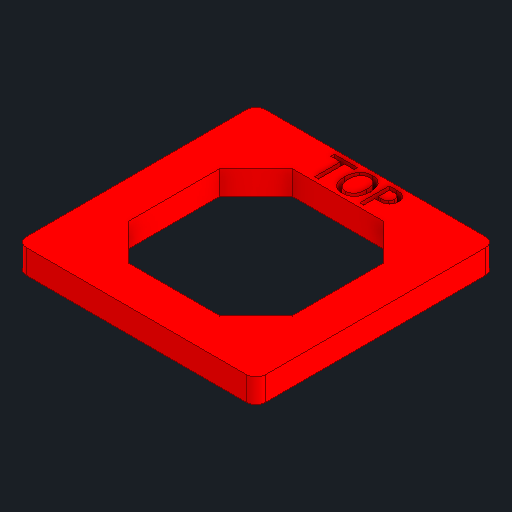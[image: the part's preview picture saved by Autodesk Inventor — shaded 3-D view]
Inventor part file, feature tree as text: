
AUTODESK INVENTOR PART (.ipt)
format: ipt  version: 2023.4 (Build 274418000, 418)  size: 544,256 bytes
history: native  units: mm
features: extrude x9, projected_geometry x9, chamfer x3, fillet x1, pattern_circular x1, sketch x1
ambient origin geometry x8: Origin, YZ Plane, XZ Plane, XY Plane, X Axis, Y Axis, Z Axis, Center Point
bodies: Solid1 (feature_tree)
feature tree (24):
  extrude  "Extrusion1"  Depth=49.8mm
  extrude  "Extrusion2"  Depth=7.85mm
  chamfer  "Chamfer1"  Distance=3.0mm
  fillet  "Fillet1"  Radius=3.0mm
  chamfer  "Chamfer2"  Distance=3.75mm
  extrude  "Extrusion3"  Depth=4.2125mm
  extrude  "Extrusion4"  Depth=0.675mm
  extrude  "Extrusion5"  Depth=10.5mm
  pattern_circular  "Circular Pattern1"  [2 undecoded]
  extrude  "Extrusion6"  Depth=4.1mm
  extrude  "Extrusion7"  Depth=4.145mm
  chamfer  "Chamfer3"  Distance=7.85mm
  extrude  "Extrusion8"  Depth=7.85mm
  extrude  "Extrusion9"  Depth=5.5mm
  sketch  "Sketch2"  dims[d0=49.8mm d1=49.8mm d2=7.85mm d3=3.0mm d4=3.0mm d5=3.75mm d6=4.2125mm d7=0.675mm d8=10.5mm d9=10.5mm d10=4.1mm d11=4.145mm d12=7.85mm d13=7.85mm d14=5.5mm d15=5.5mm d16=40.0mm d18=360.0deg d20=7.7mm d21=0.0mm d22=2.2mm d23=0.0mm d24=5.5mm d25=2.0mm d26=45.0deg d27=2.0mm d28=0.025mm d29=2.0mm d30=45.0deg d31=3.0mm d32=0.0mm d33=3.0mm d34=0.0mm d35=0.75mm d36=0.0mm d37=40.0mm d38=360.0deg d40=2.2mm d41=0.0mm d42=5.7mm d43=0.0mm d44=7.5mm d45=2.0mm d46=45.0deg d47=2.7mm d48=0.0mm d49=20.0mm d50=2.5mm d51=0.0mm]
  projected_geometry  "Projected Loop2"
  projected_geometry  "Projected Loop3"
  projected_geometry  "Projected Loop4"
  projected_geometry  "Projected Loop5"
  projected_geometry  "Projected Loop6"
  projected_geometry  "Projected Loop7"
  projected_geometry  "Projected Loop8"
  projected_geometry  "Projected Loop9"
  projected_geometry  "Projected Loop10"
note: 2 required parameter values undecoded (feature->parameter linkage not recoverable at this tier; creation-order binding heuristic only, values carry confidence <= 0.55)
